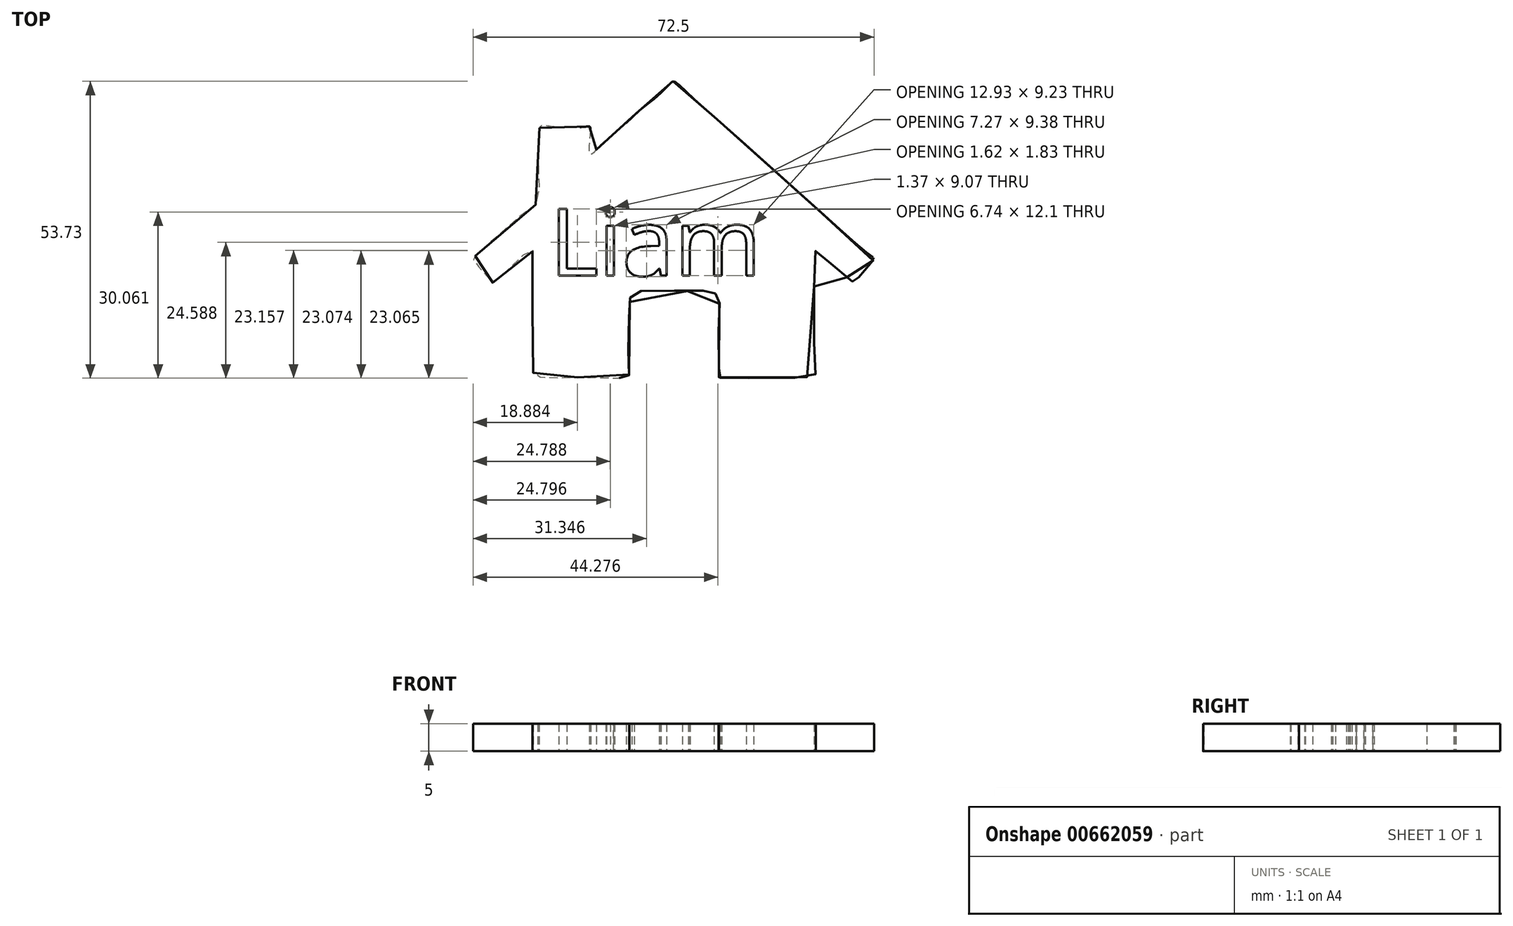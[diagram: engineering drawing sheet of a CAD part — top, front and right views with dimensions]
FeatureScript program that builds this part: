
annotation { "Feature Type Name" : "Feature", "Feature Type Description" : "" }
export const myFeature = defineFeature(function(context is Context, id is Id, definition is map)
    precondition{}
    {
        {
            var Q0;
            Q0=qCreatedBy(makeId("Top.planeOp"),FACE);
            var sketch = newSketch(context, id + "F0", { "sketchPlane" : qUnion([Q0])});
            skFitSpline(sketch, "E0", {"points": [v(-60.55, 48.41) * mm, v(-60.72, 35.71) * mm, v(-62.22, 33.87) * mm, v(-71.84, 25.6) * mm, v(-72.54, 24.9) * mm, v(-72.57, 24.75) * mm, v(-72.4, 24.38) * mm, v(-72.18, 24.1) * mm, v(-68.97, 20.35) * mm, v(-68.55, 20.52) * mm, v(-61.91, 26.61) * mm, v(-61.82, 26.14) * mm, v(-61.8, 18.16) * mm, v(-61.87, 15.33) * mm, v(-61.75, 6.94) * mm, v(-61.64, 4) * mm, v(-60.38, 3.3) * mm, v(-55.53, 3.25) * mm, v(-51.2, 3.29) * mm, v(-44.36, 3.23) * mm, v(-44.35, 3.5) * mm, v(-44.44, 12.31) * mm, v(-44.13, 17.83) * mm, v(-43.15, 18.78) * mm, v(-31.89, 18.93) * mm, v(-29.35, 18.87) * mm, v(-28.1, 17.63) * mm, v(-28.1, 15.8) * mm, v(-28.1, 3.62) * mm, v(-28.1, 3.25) * mm, v(-27.37, 3.22) * mm, v(-11.18, 3.44) * mm, v(-10.72, 4.9) * mm, v(-10.63, 26.3) * mm, v(-10.45, 26.22) * mm, v(-3.77, 20.53) * mm, v(-3.54, 20.7) * mm, v(-2.7, 21.53) * mm, v(-0.4, 24.25) * mm, v(-0.1, 24.58) * mm, v(-0.1, 24.86) * mm, v(-0.7, 25.3) * mm, v(-22.2, 44.42) * mm, v(-33.34, 54.33) * mm, v(-36.1, 56.8) * mm, v(-36.57, 56.78) * mm, v(-38.82, 54.57) * mm, v(-42.6, 51.47) * mm, v(-46.16, 48.14) * mm, v(-49.76, 45.06) * mm, v(-51.33, 43.6) * mm, v(-51.52, 45.29) * mm, v(-51.42, 48.54) * mm, v(-52.17, 48.66) * mm, v(-58.72, 48.7) * mm, v(-60.55, 48.41) * mm]});
            skText(sketch, "E1", { "text": "Liam\n", "fontName": "OpenSans-Regular.ttf"});
            const initialGuessF0  = {"E1": [-0.05872, 0.02167, 1, 0, 0.0122]};
            skSetInitialGuess(sketch, initialGuessF0);
            skSolve(sketch);
        }
        {
            var Q0;
            Q0 = qSketchRegion(id + "F0", true);
            extrude(context, id + "F1", {"entities" : qUnion([Q0]), "depth" : 5 * mm, "offsetDistance" : 25.4 * mm});
        }
    });
